# Revit family: Current FMLBY revit family
name_source: partatom
category: Mechanical Equipment
revit_build: Autodesk Revit 2018 (Build: 20170223_1515(x64)
units: mm (PartAtom-declared; Revit-internal decimal feet)

## family parameters
Always vertical = Yes
Cut with Voids When Loaded = No
OmniClass Number = 23.75.70.17.31
OmniClass Title = Induction Units
Part Type = Normal
Room Calculation Point = No
Round Connector Dimension = Use Diameter
Shared = No
Work Plane-Based = No

## types (5) — shared parameters
0.5 inch Female NPT Stub coil Connection = No
0.5 inch Male NPT Stub Coil Connection = No
0.5 inch SWT Stub Coil Connection = Yes
2 Pipe Coil Configuration = Yes
2 or 4 pipe = 2
4 Pipe Coil Configuration = No
Architectural Design Manual = http://www.activechilledbeam.com
Assembly Code = D3040100
Atmospheric Pressure = 0.00 in-wg
CWF = 0 GPM
CWPD = 0.00 ftH2O
Cooling Primary Air Dry Bulb = -460 °F
Cooling Primary Air Wet Bulb = -460 °F
Cooling Room Dry Bulb = -460 °F
Cooling Supply Air Temperature = -460 °F
Damper = Yes
Description = Chilled Beam
Floor Mounted = Yes
HWF = 0 GPM
HWPD = 0.00 ftH2O
Heating Primary Air Dry Bulb = -460 °F
Heating Room Dry Bulb = -460 °F
Heating Supply Air Temperature = -460 °F
Latent Cooling = 0.0 Btu/h
Lint Screen = Yes
Manufacturer = Dadanco
Model = FLMBY
Net Unit Cooling Sensible = 0.0 Btu/h
Net Unit Heating Sensible = 0.0 Btu/h
PA = 0 CFM
PASP = 0.00 in-wg
Pipe Coil Inlet = 2 Pipe Coi, 0.5 inch SWT Stub Coil Connection
Pipe Coil Outlet = 2 Pipe Coi, 0.5 inch SWT Stub Coil Connection
Primary Air Inlet Size = 0' - 4"
Revision Date = 07/19/2010
SCHW Temp Out = -460 °F
SCHW Temperature = -460 °F
SHHW Temp Out = -460 °F
SHHW Temperature = -460 °F
Screen Material = Metal-Dadanco-Aluminum-Screen
Secondary Air Sensible Cooling = 0.0 Btu/h
Secondary Air Sensible Heating = 0.0 Btu/h
Supply Air = 0 CFM
Total Cooling Capacity = 0.0 Btu/h
URL = http://www.dadanco.com
Unit Height = 0' - 11 3/4"
Unit Width = 0' - 8 3/4"
Wall Mounted = No
zero-valued in all types: Cooling Room Relative Humidity

## per-type parameters (varying)
| type | Coil Length | Housing Material | Nominal Unit Length | Overall Unit Length | Type Comments | Weight |
| 2' Nominal Length | 2' - 0" | Metal-Dadanco-Steel-Galvanized | 2' - 0" | 2' - 4" | MPT Stub, 2 Pipe Coil Connection, Damper and Lint Screen Available | 25 lb |
| 3' Nominal Length | 2' - 8" | Metal-Dadanco-Aluminum-Bone White | 3' - 0" | 3' - 0" |  | 33 lb |
| 4' Nominal Length | 3' - 4" | Metal-Dadanco-Aluminum-Bone White | 4' - 0" | 3' - 8" |  | 40 lb |
| 5' Nominal Length | 4' - 4" | Metal-Dadanco-Aluminum-Bone White | 5' - 0" | 4' - 8" |  | 47 lb |
| 6' Nominal Length | 5' - 4" | Metal-Dadanco-Aluminum-Bone White | 6' - 0" | 5' - 8" |  | 54 lb |

## geometry (parser evidence)
native form markers: Sweep x1
no freeform markers — native parametric forms only
